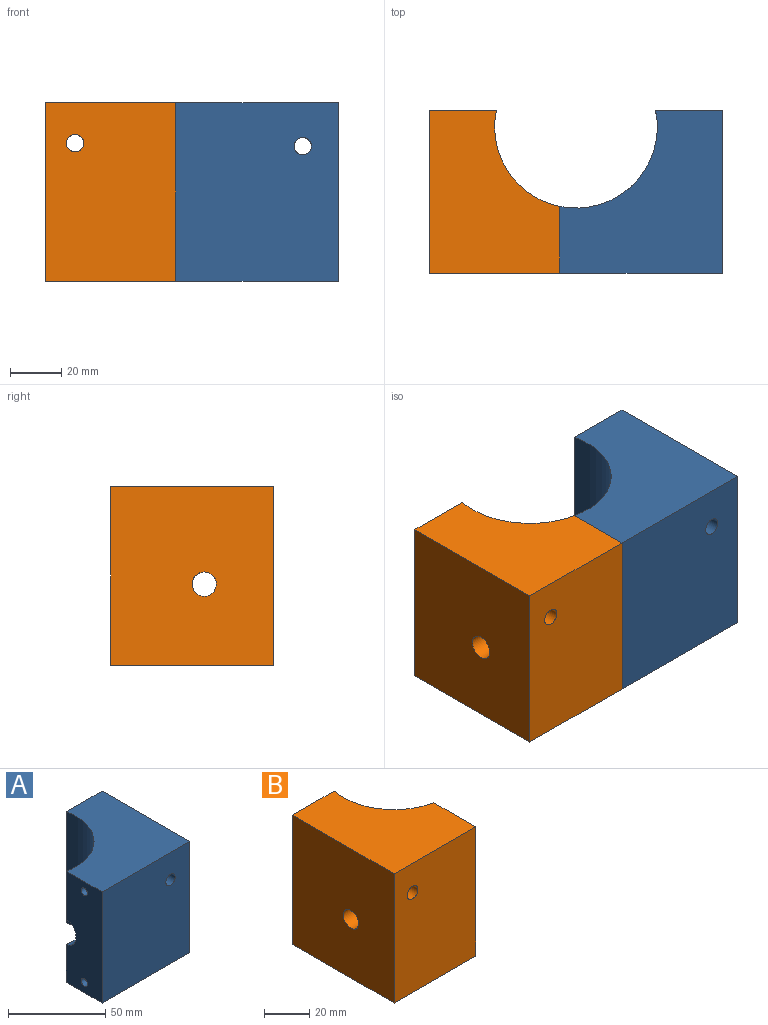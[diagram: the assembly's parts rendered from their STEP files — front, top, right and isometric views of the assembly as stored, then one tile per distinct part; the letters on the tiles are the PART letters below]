
ASSEMBLY  parts=2 mates=1
PART A: 11 faces, bbox 63.5x63.5x69.9 mm
  f0: plane 63.5x63.5mm, normal (0,0,1), area 2799.7mm2, adj f2,f3,f4,f5,f7
  f1: plane 63.5x63.5mm, normal (0,0,-1), area 2799.7mm2, adj f2,f3,f4,f5,f7
  f2: cylinder r=31.75mm len=69.85mm, axis (0,0,-1), area 3919.6mm2, adj f0,f1,f3,f6,f7
  f3: plane 69.85x26.04mm, normal (-1,0,0), area 1703.3mm2, adj f0,f1,f2,f4,f6,f9,f10
  f4: plane 69.85x63.5mm, normal (0,-1,0), area 4399.6mm2, adj f0,f1,f3,f5,f8
  f5: plane 69.85x63.5mm, normal (1,0,0), area 4205.8mm2, adj f0,f1,f4,f6,f7,f9,f10
  f6: cylinder r=7.94mm len=63.5mm, axis (1,0,0), area 2497.6mm2, adj f2,f3,f5
  f7: plane 69.85x26.04mm, normal (0,1,0), area 1783.1mm2, adj f0,f1,f2,f5,f8
  f8: cylinder r=3.38mm len=63.5mm, axis (0,-1,0), area 1347.8mm2, adj f4,f7
  f9: cylinder r=2.25mm len=63.5mm, axis (1,0,0), area 896.9mm2, adj f3,f5
  f10: cylinder r=2.25mm len=63.5mm, axis (1,0,0), area 896.9mm2, adj f3,f5
PART B: 13 faces, bbox 50.8x63.5x69.9 mm
  f0: plane 69.85x63.5mm, normal (-1,0,0), area 4364.2mm2, adj f1,f2,f3,f6,f7
  f1: plane 63.5x50.8mm, normal (0,0,-1), area 2474.4mm2, adj f0,f3,f4,f5,f7
  f2: plane 63.5x50.8mm, normal (0,0,1), area 2474.4mm2, adj f0,f3,f4,f5,f7
  f3: plane 69.85x50.8mm, normal (0,-1,0), area 3512.5mm2, adj f0,f1,f2,f4,f8
  f4: plane 69.85x26.04mm, normal (1,0,0), area 1773.6mm2, adj f1,f2,f3,f5,f6,f9,f11
  f5: cylinder r=31.75mm len=69.85mm, axis (0,0,-1), area 3368mm2, adj f1,f2,f4,f6,f7
  f6: cylinder r=4.76mm len=50.8mm, axis (1,0,0), area 1368.9mm2, adj f0,f4,f5
  f7: plane 69.85x26.04mm, normal (0,1,0), area 1783.1mm2, adj f0,f1,f2,f5,f8
  f8: cylinder r=3.38mm len=63.5mm, axis (0,-1,0), area 1347.8mm2, adj f3,f7
  f9: cylinder r=1.73mm len=37.94mm, axis (1,0,0), area 411.8mm2, adj f4,f10
  f10: cone r=0mm half-angle=59deg, axis (1,0,0), area 10.9mm2, adj f9
  f11: cylinder r=1.73mm len=37.94mm, axis (1,0,0), area 411.8mm2, adj f4,f12
  f12: cone r=0mm half-angle=59deg, axis (1,0,0), area 10.9mm2, adj f11
PLACE A at identity fixed
PLACE B at identity
MATE fastened A.f9 <-> B.f9  axis (-1,0,0) through (-6.35,-44.13,101.6)mm
